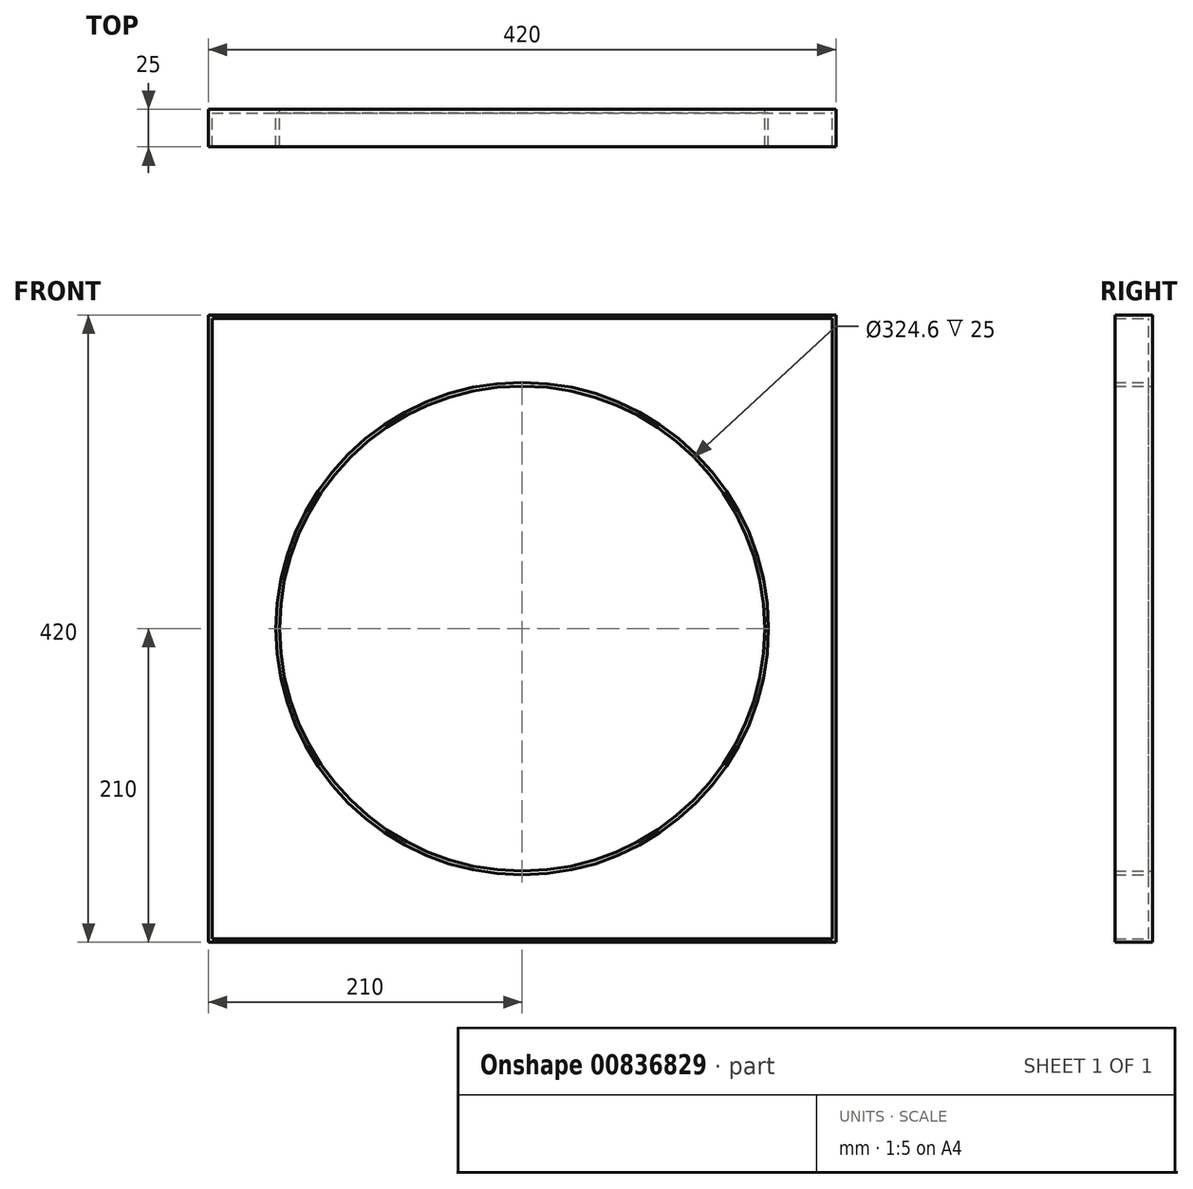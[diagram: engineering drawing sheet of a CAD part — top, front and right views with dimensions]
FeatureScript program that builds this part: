
annotation { "Feature Type Name" : "Feature", "Feature Type Description" : "" }
export const myFeature = defineFeature(function(context is Context, id is Id, definition is map)
    precondition{}
    {
        {
            var Q0;
            Q0=qCreatedBy(makeId("Front.planeOp"),FACE);
            var sketch = newSketch(context, id + "F0", { "sketchPlane" : qUnion([Q0])});
            skLineSegment(sketch, "E0.bottom", {"start": v(-210, -210) * mm, "end": v(210, -210) * mm});
            skLineSegment(sketch, "E0.top", {"start": v(-210, 210) * mm, "end": v(210, 210) * mm});
            skLineSegment(sketch, "E0.left", {"start": v(-210, -210) * mm, "end": v(-210, 210) * mm});
            skLineSegment(sketch, "E0.right", {"start": v(210, -210) * mm, "end": v(210, 210) * mm});
            skPoint(sketch, "E0.middle", {"position": v(0, 0) * mm});
            skCircle(sketch, "E1", {"center": v(0, 0) * mm, "radius": 162.3 * mm});
            skLineSegment(sketch, "E2.bottom", {"start": v(18.41, 100.05) * mm, "end": v(35.27, 100.05) * mm});
            skLineSegment(sketch, "E2.top", {"start": v(18.41, 104.49) * mm, "end": v(35.27, 104.49) * mm});
            skLineSegment(sketch, "E2.left", {"start": v(18.41, 100.05) * mm, "end": v(18.41, 104.49) * mm});
            skLineSegment(sketch, "E2.right", {"start": v(35.27, 100.05) * mm, "end": v(35.27, 104.49) * mm});
            skPoint(sketch, "E2.middle", {"position": v(26.84, 102.27) * mm});
            skSolve(sketch);
        }
        {
            var Q0;
            Q0 = qSketchRegion(id + "F0", true);
            extrude(context, id + "F1", {"entities" : qUnion([Q0]), "depth" : 25 * mm, "offsetDistance" : 25 * mm});
        }
        {
            var Q0;
            Q0 = qSketchRegion(id + "F0", true);
            extrude(context, id + "F2", {"entities" : qUnion([Q0]), "operationType" : NewBodyOperationType.ADD, "depth" : 25 * mm, "offsetDistance" : 25 * mm});
        }
        {
            var Q0;
            Q0=makeQuery(id+"F1.opExtrude","CAP_FACE",FACE,{"disambiguationData":[OSD([sQuery(id+"F0.wireOp",EDGE,"E0.bottom"),sQuery(id+"F0.wireOp",EDGE,"E0.top"),sQuery(id+"F0.wireOp",EDGE,"E0.left"),sQuery(id+"F0.wireOp",EDGE,"E0.right"),sQuery(id+"F0.wireOp",EDGE,"E1")])],"isStart":false});
            shell(context, id + "F3", {"entities" : qUnion([Q0]), "thickness" : 2.5 * mm});
        }
    });
